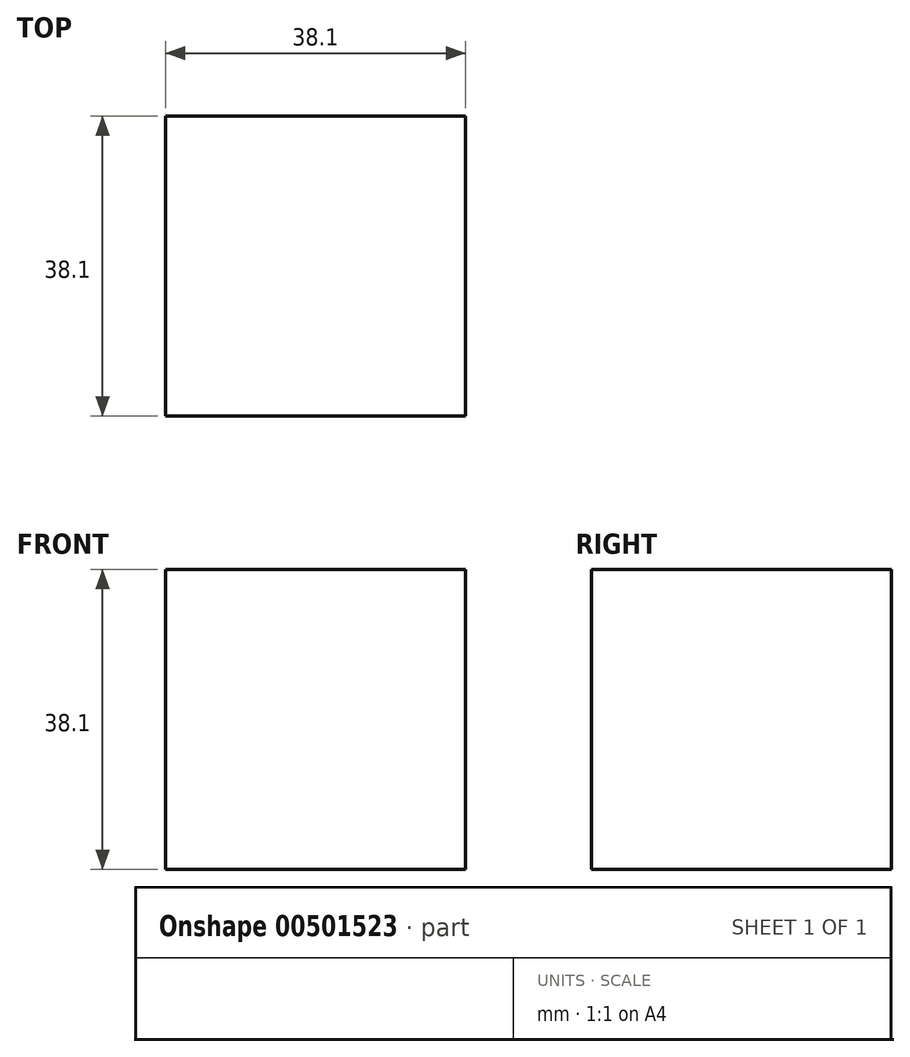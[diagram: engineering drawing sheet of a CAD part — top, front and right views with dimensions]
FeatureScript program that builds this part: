
annotation { "Feature Type Name" : "Feature", "Feature Type Description" : "" }
export const myFeature = defineFeature(function(context is Context, id is Id, definition is map)
    precondition{}
    {
        {
            var Q0;
            Q0=qCreatedBy(makeId("Top.planeOp"),FACE);
            var sketch = newSketch(context, id + "F0", { "sketchPlane" : qUnion([Q0])});
            skLineSegment(sketch, "E0.bottom", {"start": v(-19.05, 19.05) * mm, "end": v(19.05, 19.05) * mm});
            skLineSegment(sketch, "E0.top", {"start": v(-19.05, -19.05) * mm, "end": v(19.05, -19.05) * mm});
            skLineSegment(sketch, "E0.left", {"start": v(-19.05, 19.05) * mm, "end": v(-19.05, -19.05) * mm});
            skLineSegment(sketch, "E0.right", {"start": v(19.05, 19.05) * mm, "end": v(19.05, -19.05) * mm});
            skPoint(sketch, "E0.middle", {"position": v(0, 0) * mm});
            skSolve(sketch);
        }
        {
            var Q0;
            Q0 = qSketchRegion(id + "F0", true);
            extrude(context, id + "F1", {"entities" : qUnion([Q0]), "offsetDistance" : 25.4 * mm, "depth" : 38.1 * mm});
        }
    });
